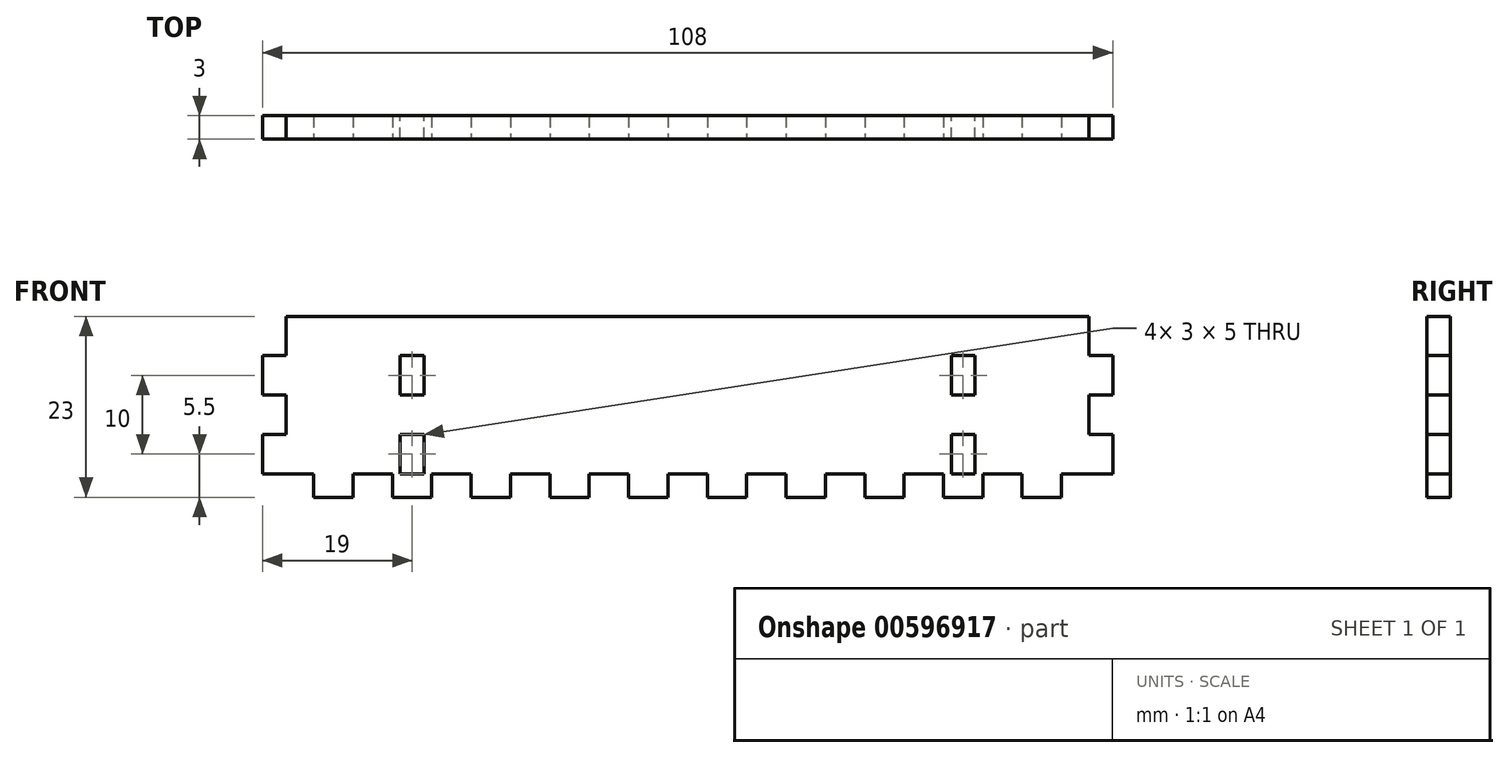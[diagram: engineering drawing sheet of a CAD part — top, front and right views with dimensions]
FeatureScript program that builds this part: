
annotation { "Feature Type Name" : "Feature", "Feature Type Description" : "" }
export const myFeature = defineFeature(function(context is Context, id is Id, definition is map)
    precondition{}
    {
        {
            var Q0;
            Q0=qCreatedBy(makeId("Front.planeOp"),FACE);
            var sketch = newSketch(context, id + "F0", { "sketchPlane" : qUnion([Q0])});
            skLineSegment(sketch, "E0.bottom", {"start": v(51, 20) * mm, "end": v(-51, 20) * mm});
            skLineSegment(sketch, "E0.top", {"start": v(51, -20) * mm, "end": v(-51, -20) * mm});
            skLineSegment(sketch, "E0.left", {"start": v(51, 20) * mm, "end": v(51, -20) * mm});
            skLineSegment(sketch, "E0.right", {"start": v(-51, 20) * mm, "end": v(-51, -20) * mm});
            skPoint(sketch, "E0.middle", {"position": v(0, 0) * mm});
            skSolve(sketch);
        }
        {
            var Q0;
            Q0=qSketchRegion(id+"F0",true);
            extrude(context, id + "F1", {"entities" : qUnion([Q0]), "depth" : 3 * mm, "offsetDistance" : 25 * mm});
        }
        {
            var Q0;
            Q0=makeQuery(id+"F1.opExtrude","CAP_FACE",FACE,{"disambiguationData":[OSD([sQuery(id+"F0.wireOp",EDGE,"E0.bottom"),sQuery(id+"F0.wireOp",EDGE,"E0.top"),sQuery(id+"F0.wireOp",EDGE,"E0.left"),sQuery(id+"F0.wireOp",EDGE,"E0.right")])],"isStart":false});
            var sketch = newSketch(context, id + "F2", { "sketchPlane" : qUnion([Q0])});
            skLineSegment(sketch, "E1.bottom", {"start": v(-51, -20) * mm, "end": v(-54, -20) * mm});
            skLineSegment(sketch, "E1.top", {"start": v(-51, -15) * mm, "end": v(-54, -15) * mm});
            skLineSegment(sketch, "E1.left", {"start": v(-51, -20) * mm, "end": v(-51, -15) * mm});
            skLineSegment(sketch, "E1.right", {"start": v(-54, -20) * mm, "end": v(-54, -15) * mm});
            skLineSegment(sketch, "E2.0.1.0", {"start": v(-51, -5) * mm, "end": v(-54, -5) * mm});
            skLineSegment(sketch, "E2.0.1.1", {"start": v(-54, -10) * mm, "end": v(-54, -5) * mm});
            skLineSegment(sketch, "E2.0.1.2", {"start": v(-51, -10) * mm, "end": v(-51, -5) * mm});
            skLineSegment(sketch, "E2.0.1.3", {"start": v(-51, -10) * mm, "end": v(-54, -10) * mm});
            skLineSegment(sketch, "E2.0.2.0", {"start": v(-51, 5) * mm, "end": v(-54, 5) * mm});
            skLineSegment(sketch, "E2.0.2.1", {"start": v(-54, 0) * mm, "end": v(-54, 5) * mm});
            skLineSegment(sketch, "E2.0.2.2", {"start": v(-51, 0) * mm, "end": v(-51, 5) * mm});
            skLineSegment(sketch, "E2.0.2.3", {"start": v(-51, 0) * mm, "end": v(-54, 0) * mm});
            skLineSegment(sketch, "E2.0.3.0", {"start": v(-51, 15) * mm, "end": v(-54, 15) * mm});
            skLineSegment(sketch, "E2.0.3.1", {"start": v(-54, 10) * mm, "end": v(-54, 15) * mm});
            skLineSegment(sketch, "E2.0.3.2", {"start": v(-51, 10) * mm, "end": v(-51, 15) * mm});
            skLineSegment(sketch, "E2.0.3.3", {"start": v(-51, 10) * mm, "end": v(-54, 10) * mm});
            skLineSegment(sketch, "E2.direction1", {"start": v(-54, -15) * mm, "end": v(-29, -15) * mm, "construction": true});
            skLineSegment(sketch, "E2.direction2", {"start": v(-54, -15) * mm, "end": v(-54, -5) * mm, "construction": true});
            skLineSegment(sketch, "E3.MirrorCS", {"start": v(54, -10) * mm, "end": v(54, -5) * mm});
            skLineSegment(sketch, "E4.MirrorCS", {"start": v(51, -5) * mm, "end": v(54, -5) * mm});
            skLineSegment(sketch, "E5.MirrorCS", {"start": v(51, -20) * mm, "end": v(51, -15) * mm});
            skLineSegment(sketch, "E6.MirrorCS", {"start": v(54, 10) * mm, "end": v(54, 15) * mm});
            skLineSegment(sketch, "E7.MirrorCS", {"start": v(51, -20) * mm, "end": v(54, -20) * mm});
            skLineSegment(sketch, "E8.MirrorCS", {"start": v(51, -15) * mm, "end": v(54, -15) * mm});
            skLineSegment(sketch, "E9.MirrorCS", {"start": v(54, -20) * mm, "end": v(54, -15) * mm});
            skLineSegment(sketch, "E10.MirrorCS", {"start": v(51, 15) * mm, "end": v(54, 15) * mm});
            skLineSegment(sketch, "E11.MirrorCS", {"start": v(51, 10) * mm, "end": v(54, 10) * mm});
            skLineSegment(sketch, "E12.MirrorCS", {"start": v(54, -15) * mm, "end": v(54, -5) * mm, "construction": true});
            skLineSegment(sketch, "E13.MirrorCS", {"start": v(51, 10) * mm, "end": v(51, 15) * mm});
            skLineSegment(sketch, "E14.MirrorCS", {"start": v(54, 0) * mm, "end": v(54, 5) * mm});
            skLineSegment(sketch, "E15.MirrorCS", {"start": v(51, 0) * mm, "end": v(51, 5) * mm});
            skLineSegment(sketch, "E16.MirrorCS", {"start": v(51, 0) * mm, "end": v(54, 0) * mm});
            skLineSegment(sketch, "E17.MirrorCS", {"start": v(51, -10) * mm, "end": v(51, -5) * mm});
            skLineSegment(sketch, "E18.MirrorCS", {"start": v(51, -10) * mm, "end": v(54, -10) * mm});
            skLineSegment(sketch, "E19.MirrorCS", {"start": v(51, 5) * mm, "end": v(54, 5) * mm});
            skSolve(sketch);
        }
        {
            var Q0;
            Q0=qSketchRegion(id+"F2",true);
            extrude(context, id + "F3", {"entities" : qUnion([Q0]), "operationType" : NewBodyOperationType.ADD, "oppositeDirection" : true, "depth" : 3 * mm, "offsetDistance" : 25 * mm});
        }
        {
            var Q0;
            Q0=makeQuery(id+"F3.boolean.opBoolean","MERGE",FACE,{"derivedFrom":[makeQuery(id+"F1.opExtrude","CAP_FACE",FACE,{"disambiguationData":[OSD([sQuery(id+"F0.wireOp",EDGE,"E0.bottom"),sQuery(id+"F0.wireOp",EDGE,"E0.top"),sQuery(id+"F0.wireOp",EDGE,"E0.left"),sQuery(id+"F0.wireOp",EDGE,"E0.right")])],"isStart":false}),makeQuery(id+"F3.opExtrude","CAP_FACE",FACE,{"disambiguationData":[OSD([sQuery(id+"F2.wireOp",EDGE,"E1.bottom"),sQuery(id+"F2.wireOp",EDGE,"E1.top"),sQuery(id+"F2.wireOp",EDGE,"E1.left"),sQuery(id+"F2.wireOp",EDGE,"E1.right")])],"isStart":true}),makeQuery(id+"F3.opExtrude","CAP_FACE",FACE,{"disambiguationData":[OSD([sQuery(id+"F2.wireOp",EDGE,"E2.0.1.0"),sQuery(id+"F2.wireOp",EDGE,"E2.0.1.1"),sQuery(id+"F2.wireOp",EDGE,"E2.0.1.2"),sQuery(id+"F2.wireOp",EDGE,"E2.0.1.3")])],"isStart":true}),makeQuery(id+"F3.opExtrude","CAP_FACE",FACE,{"disambiguationData":[OSD([sQuery(id+"F2.wireOp",EDGE,"E2.0.2.0"),sQuery(id+"F2.wireOp",EDGE,"E2.0.2.1"),sQuery(id+"F2.wireOp",EDGE,"E2.0.2.2"),sQuery(id+"F2.wireOp",EDGE,"E2.0.2.3")])],"isStart":true}),makeQuery(id+"F3.opExtrude","CAP_FACE",FACE,{"disambiguationData":[OSD([sQuery(id+"F2.wireOp",EDGE,"E2.0.3.0"),sQuery(id+"F2.wireOp",EDGE,"E2.0.3.1"),sQuery(id+"F2.wireOp",EDGE,"E2.0.3.2"),sQuery(id+"F2.wireOp",EDGE,"E2.0.3.3")])],"isStart":true}),makeQuery(id+"F3.opExtrude","CAP_FACE",FACE,{"disambiguationData":[OSD([sQuery(id+"F2.wireOp",EDGE,"E3.MirrorCS"),sQuery(id+"F2.wireOp",EDGE,"E4.MirrorCS"),sQuery(id+"F2.wireOp",EDGE,"E17.MirrorCS"),sQuery(id+"F2.wireOp",EDGE,"E18.MirrorCS")])],"isStart":true}),makeQuery(id+"F3.opExtrude","CAP_FACE",FACE,{"disambiguationData":[OSD([sQuery(id+"F2.wireOp",EDGE,"E5.MirrorCS"),sQuery(id+"F2.wireOp",EDGE,"E7.MirrorCS"),sQuery(id+"F2.wireOp",EDGE,"E8.MirrorCS"),sQuery(id+"F2.wireOp",EDGE,"E9.MirrorCS")])],"isStart":true}),makeQuery(id+"F3.opExtrude","CAP_FACE",FACE,{"disambiguationData":[OSD([sQuery(id+"F2.wireOp",EDGE,"E6.MirrorCS"),sQuery(id+"F2.wireOp",EDGE,"E10.MirrorCS"),sQuery(id+"F2.wireOp",EDGE,"E11.MirrorCS"),sQuery(id+"F2.wireOp",EDGE,"E13.MirrorCS")])],"isStart":true}),makeQuery(id+"F3.opExtrude","CAP_FACE",FACE,{"disambiguationData":[OSD([sQuery(id+"F2.wireOp",EDGE,"E14.MirrorCS"),sQuery(id+"F2.wireOp",EDGE,"E15.MirrorCS"),sQuery(id+"F2.wireOp",EDGE,"E16.MirrorCS"),sQuery(id+"F2.wireOp",EDGE,"E19.MirrorCS")])],"isStart":true})]});
            var sketch = newSketch(context, id + "F4", { "sketchPlane" : qUnion([Q0])});
            skLineSegment(sketch, "E20", {"start": v(0, -20) * mm, "end": v(0, -23) * mm, "construction": true});
            skPoint(sketch, "E20.endSnap0", {"position": v(0, -20) * mm});
            skLineSegment(sketch, "E21", {"start": v(0, -23) * mm, "end": v(2.5, -23) * mm, "construction": true});
            skLineSegment(sketch, "E22.bottom", {"start": v(2.5, -23) * mm, "end": v(7.5, -23) * mm});
            skLineSegment(sketch, "E22.top", {"start": v(2.5, -20) * mm, "end": v(7.5, -20) * mm});
            skLineSegment(sketch, "E22.left", {"start": v(2.5, -23) * mm, "end": v(2.5, -20) * mm});
            skLineSegment(sketch, "E22.right", {"start": v(7.5, -23) * mm, "end": v(7.5, -20) * mm});
            skLineSegment(sketch, "E23.1.0.0", {"start": v(12.5, -23) * mm, "end": v(17.5, -23) * mm});
            skLineSegment(sketch, "E23.1.0.1", {"start": v(12.5, -23) * mm, "end": v(12.5, -20) * mm});
            skLineSegment(sketch, "E23.1.0.2", {"start": v(17.5, -23) * mm, "end": v(17.5, -20) * mm});
            skLineSegment(sketch, "E23.1.0.3", {"start": v(12.5, -20) * mm, "end": v(17.5, -20) * mm});
            skLineSegment(sketch, "E23.2.0.0", {"start": v(22.5, -23) * mm, "end": v(27.5, -23) * mm});
            skLineSegment(sketch, "E23.2.0.1", {"start": v(22.5, -23) * mm, "end": v(22.5, -20) * mm});
            skLineSegment(sketch, "E23.2.0.2", {"start": v(27.5, -23) * mm, "end": v(27.5, -20) * mm});
            skLineSegment(sketch, "E23.2.0.3", {"start": v(22.5, -20) * mm, "end": v(27.5, -20) * mm});
            skLineSegment(sketch, "E23.3.0.0", {"start": v(32.5, -23) * mm, "end": v(37.5, -23) * mm});
            skLineSegment(sketch, "E23.3.0.1", {"start": v(32.5, -23) * mm, "end": v(32.5, -20) * mm});
            skLineSegment(sketch, "E23.3.0.2", {"start": v(37.5, -23) * mm, "end": v(37.5, -20) * mm});
            skLineSegment(sketch, "E23.3.0.3", {"start": v(32.5, -20) * mm, "end": v(37.5, -20) * mm});
            skLineSegment(sketch, "E23.4.0.0", {"start": v(42.5, -23) * mm, "end": v(47.5, -23) * mm});
            skLineSegment(sketch, "E23.4.0.1", {"start": v(42.5, -23) * mm, "end": v(42.5, -20) * mm});
            skLineSegment(sketch, "E23.4.0.2", {"start": v(47.5, -23) * mm, "end": v(47.5, -20) * mm});
            skLineSegment(sketch, "E23.4.0.3", {"start": v(42.5, -20) * mm, "end": v(47.5, -20) * mm});
            skLineSegment(sketch, "E23.direction1", {"start": v(2.5, -23) * mm, "end": v(12.5, -23) * mm, "construction": true});
            skLineSegment(sketch, "E24.MirrorCS", {"start": v(-27.5, -23) * mm, "end": v(-27.5, -20) * mm});
            skLineSegment(sketch, "E25.MirrorCS", {"start": v(-22.5, -23) * mm, "end": v(-22.5, -20) * mm});
            skLineSegment(sketch, "E26.MirrorCS", {"start": v(-17.5, -23) * mm, "end": v(-17.5, -20) * mm});
            skLineSegment(sketch, "E27.MirrorCS", {"start": v(-12.5, -23) * mm, "end": v(-12.5, -20) * mm});
            skLineSegment(sketch, "E28.MirrorCS", {"start": v(-7.5, -23) * mm, "end": v(-7.5, -20) * mm});
            skLineSegment(sketch, "E29.MirrorCS", {"start": v(-2.5, -23) * mm, "end": v(-2.5, -20) * mm});
            skLineSegment(sketch, "E30.MirrorCS", {"start": v(-32.5, -23) * mm, "end": v(-32.5, -20) * mm});
            skLineSegment(sketch, "E31.MirrorCS", {"start": v(-47.5, -23) * mm, "end": v(-47.5, -20) * mm});
            skLineSegment(sketch, "E32.MirrorCS", {"start": v(-37.5, -23) * mm, "end": v(-37.5, -20) * mm});
            skLineSegment(sketch, "E33.MirrorCS", {"start": v(-42.5, -23) * mm, "end": v(-42.5, -20) * mm});
            skLineSegment(sketch, "E34.MirrorCS", {"start": v(-2.5, -23) * mm, "end": v(-7.5, -23) * mm});
            skLineSegment(sketch, "E35.MirrorCS", {"start": v(-32.5, -20) * mm, "end": v(-37.5, -20) * mm});
            skLineSegment(sketch, "E36.MirrorCS", {"start": v(-42.5, -20) * mm, "end": v(-47.5, -20) * mm});
            skLineSegment(sketch, "E37.MirrorCS", {"start": v(-22.5, -23) * mm, "end": v(-27.5, -23) * mm});
            skLineSegment(sketch, "E38.MirrorCS", {"start": v(-12.5, -20) * mm, "end": v(-17.5, -20) * mm});
            skLineSegment(sketch, "E39.MirrorCS", {"start": v(-12.5, -23) * mm, "end": v(-17.5, -23) * mm});
            skLineSegment(sketch, "E40.MirrorCS", {"start": v(-2.5, -20) * mm, "end": v(-7.5, -20) * mm});
            skLineSegment(sketch, "E41.MirrorCS", {"start": v(-32.5, -23) * mm, "end": v(-37.5, -23) * mm});
            skLineSegment(sketch, "E42.MirrorCS", {"start": v(-22.5, -20) * mm, "end": v(-27.5, -20) * mm});
            skLineSegment(sketch, "E43.MirrorCS", {"start": v(-42.5, -23) * mm, "end": v(-47.5, -23) * mm});
            skLineSegment(sketch, "E44.MirrorCS", {"start": v(-2.5, -23) * mm, "end": v(-12.5, -23) * mm, "construction": true});
            skSolve(sketch);
        }
        {
            var Q0;
            Q0=qSketchRegion(id+"F4",true);
            extrude(context, id + "F5", {"entities" : qUnion([Q0]), "operationType" : NewBodyOperationType.ADD, "oppositeDirection" : true, "depth" : 3 * mm, "offsetDistance" : 25 * mm});
        }
        {
            var Q0;
            Q0=makeQuery(id+"F5.boolean.opBoolean","MERGE",FACE,{"derivedFrom":[makeQuery(id+"F3.boolean.opBoolean","MERGE",FACE,{"derivedFrom":[makeQuery(id+"F1.opExtrude","CAP_FACE",FACE,{"disambiguationData":[OSD([sQuery(id+"F0.wireOp",EDGE,"E0.bottom"),sQuery(id+"F0.wireOp",EDGE,"E0.top"),sQuery(id+"F0.wireOp",EDGE,"E0.left"),sQuery(id+"F0.wireOp",EDGE,"E0.right")])],"isStart":false}),makeQuery(id+"F3.opExtrude","CAP_FACE",FACE,{"disambiguationData":[OSD([sQuery(id+"F2.wireOp",EDGE,"E1.bottom"),sQuery(id+"F2.wireOp",EDGE,"E1.top"),sQuery(id+"F2.wireOp",EDGE,"E1.left"),sQuery(id+"F2.wireOp",EDGE,"E1.right")])],"isStart":true}),makeQuery(id+"F3.opExtrude","CAP_FACE",FACE,{"disambiguationData":[OSD([sQuery(id+"F2.wireOp",EDGE,"E2.0.1.0"),sQuery(id+"F2.wireOp",EDGE,"E2.0.1.1"),sQuery(id+"F2.wireOp",EDGE,"E2.0.1.2"),sQuery(id+"F2.wireOp",EDGE,"E2.0.1.3")])],"isStart":true}),makeQuery(id+"F3.opExtrude","CAP_FACE",FACE,{"disambiguationData":[OSD([sQuery(id+"F2.wireOp",EDGE,"E2.0.2.0"),sQuery(id+"F2.wireOp",EDGE,"E2.0.2.1"),sQuery(id+"F2.wireOp",EDGE,"E2.0.2.2"),sQuery(id+"F2.wireOp",EDGE,"E2.0.2.3")])],"isStart":true}),makeQuery(id+"F3.opExtrude","CAP_FACE",FACE,{"disambiguationData":[OSD([sQuery(id+"F2.wireOp",EDGE,"E2.0.3.0"),sQuery(id+"F2.wireOp",EDGE,"E2.0.3.1"),sQuery(id+"F2.wireOp",EDGE,"E2.0.3.2"),sQuery(id+"F2.wireOp",EDGE,"E2.0.3.3")])],"isStart":true}),makeQuery(id+"F3.opExtrude","CAP_FACE",FACE,{"disambiguationData":[OSD([sQuery(id+"F2.wireOp",EDGE,"E3.MirrorCS"),sQuery(id+"F2.wireOp",EDGE,"E4.MirrorCS"),sQuery(id+"F2.wireOp",EDGE,"E17.MirrorCS"),sQuery(id+"F2.wireOp",EDGE,"E18.MirrorCS")])],"isStart":true}),makeQuery(id+"F3.opExtrude","CAP_FACE",FACE,{"disambiguationData":[OSD([sQuery(id+"F2.wireOp",EDGE,"E5.MirrorCS"),sQuery(id+"F2.wireOp",EDGE,"E7.MirrorCS"),sQuery(id+"F2.wireOp",EDGE,"E8.MirrorCS"),sQuery(id+"F2.wireOp",EDGE,"E9.MirrorCS")])],"isStart":true}),makeQuery(id+"F3.opExtrude","CAP_FACE",FACE,{"disambiguationData":[OSD([sQuery(id+"F2.wireOp",EDGE,"E6.MirrorCS"),sQuery(id+"F2.wireOp",EDGE,"E10.MirrorCS"),sQuery(id+"F2.wireOp",EDGE,"E11.MirrorCS"),sQuery(id+"F2.wireOp",EDGE,"E13.MirrorCS")])],"isStart":true}),makeQuery(id+"F3.opExtrude","CAP_FACE",FACE,{"disambiguationData":[OSD([sQuery(id+"F2.wireOp",EDGE,"E14.MirrorCS"),sQuery(id+"F2.wireOp",EDGE,"E15.MirrorCS"),sQuery(id+"F2.wireOp",EDGE,"E16.MirrorCS"),sQuery(id+"F2.wireOp",EDGE,"E19.MirrorCS")])],"isStart":true})]}),makeQuery(id+"F5.opExtrude","CAP_FACE",FACE,{"disambiguationData":[OSD([sQuery(id+"F4.wireOp",EDGE,"E22.bottom"),sQuery(id+"F4.wireOp",EDGE,"E22.top"),sQuery(id+"F4.wireOp",EDGE,"E22.left"),sQuery(id+"F4.wireOp",EDGE,"E22.right")])],"isStart":true}),makeQuery(id+"F5.opExtrude","CAP_FACE",FACE,{"disambiguationData":[OSD([sQuery(id+"F4.wireOp",EDGE,"E23.1.0.0"),sQuery(id+"F4.wireOp",EDGE,"E23.1.0.1"),sQuery(id+"F4.wireOp",EDGE,"E23.1.0.2"),sQuery(id+"F4.wireOp",EDGE,"E23.1.0.3")])],"isStart":true}),makeQuery(id+"F5.opExtrude","CAP_FACE",FACE,{"disambiguationData":[OSD([sQuery(id+"F4.wireOp",EDGE,"E23.2.0.0"),sQuery(id+"F4.wireOp",EDGE,"E23.2.0.1"),sQuery(id+"F4.wireOp",EDGE,"E23.2.0.2"),sQuery(id+"F4.wireOp",EDGE,"E23.2.0.3")])],"isStart":true}),makeQuery(id+"F5.opExtrude","CAP_FACE",FACE,{"disambiguationData":[OSD([sQuery(id+"F4.wireOp",EDGE,"E23.3.0.0"),sQuery(id+"F4.wireOp",EDGE,"E23.3.0.1"),sQuery(id+"F4.wireOp",EDGE,"E23.3.0.2"),sQuery(id+"F4.wireOp",EDGE,"E23.3.0.3")])],"isStart":true}),makeQuery(id+"F5.opExtrude","CAP_FACE",FACE,{"disambiguationData":[OSD([sQuery(id+"F4.wireOp",EDGE,"E23.4.0.0"),sQuery(id+"F4.wireOp",EDGE,"E23.4.0.1"),sQuery(id+"F4.wireOp",EDGE,"E23.4.0.2"),sQuery(id+"F4.wireOp",EDGE,"E23.4.0.3")])],"isStart":true}),makeQuery(id+"F5.opExtrude","CAP_FACE",FACE,{"disambiguationData":[OSD([sQuery(id+"F4.wireOp",EDGE,"E24.MirrorCS"),sQuery(id+"F4.wireOp",EDGE,"E25.MirrorCS"),sQuery(id+"F4.wireOp",EDGE,"E37.MirrorCS"),sQuery(id+"F4.wireOp",EDGE,"E42.MirrorCS")])],"isStart":true}),makeQuery(id+"F5.opExtrude","CAP_FACE",FACE,{"disambiguationData":[OSD([sQuery(id+"F4.wireOp",EDGE,"E26.MirrorCS"),sQuery(id+"F4.wireOp",EDGE,"E27.MirrorCS"),sQuery(id+"F4.wireOp",EDGE,"E38.MirrorCS"),sQuery(id+"F4.wireOp",EDGE,"E39.MirrorCS")])],"isStart":true}),makeQuery(id+"F5.opExtrude","CAP_FACE",FACE,{"disambiguationData":[OSD([sQuery(id+"F4.wireOp",EDGE,"E28.MirrorCS"),sQuery(id+"F4.wireOp",EDGE,"E29.MirrorCS"),sQuery(id+"F4.wireOp",EDGE,"E34.MirrorCS"),sQuery(id+"F4.wireOp",EDGE,"E40.MirrorCS")])],"isStart":true}),makeQuery(id+"F5.opExtrude","CAP_FACE",FACE,{"disambiguationData":[OSD([sQuery(id+"F4.wireOp",EDGE,"E30.MirrorCS"),sQuery(id+"F4.wireOp",EDGE,"E32.MirrorCS"),sQuery(id+"F4.wireOp",EDGE,"E35.MirrorCS"),sQuery(id+"F4.wireOp",EDGE,"E41.MirrorCS")])],"isStart":true}),makeQuery(id+"F5.opExtrude","CAP_FACE",FACE,{"disambiguationData":[OSD([sQuery(id+"F4.wireOp",EDGE,"E31.MirrorCS"),sQuery(id+"F4.wireOp",EDGE,"E33.MirrorCS"),sQuery(id+"F4.wireOp",EDGE,"E36.MirrorCS"),sQuery(id+"F4.wireOp",EDGE,"E43.MirrorCS")])],"isStart":true})]});
            var sketch = newSketch(context, id + "F6", { "sketchPlane" : qUnion([Q0])});
            skLineSegment(sketch, "E45.bottom", {"start": v(-54, 0) * mm, "end": v(60.5, 0) * mm});
            skLineSegment(sketch, "E45.top", {"start": v(-54, 23.45) * mm, "end": v(60.5, 23.45) * mm});
            skLineSegment(sketch, "E45.left", {"start": v(-54, 0) * mm, "end": v(-54, 23.45) * mm});
            skLineSegment(sketch, "E45.right", {"start": v(60.5, 0) * mm, "end": v(60.5, 23.45) * mm});
            skSolve(sketch);
        }
        {
            var Q0;
            Q0 = qSketchRegion(id + "F6", true);
            extrude(context, id + "F7", {"entities" : qUnion([Q0]), "operationType" : NewBodyOperationType.REMOVE, "oppositeDirection" : true, "depth" : 25 * mm, "offsetDistance" : 25 * mm});
        }
        {
            var Q0;
            Q0=makeQuery(id+"F5.boolean.opBoolean","MERGE",FACE,{"derivedFrom":[makeQuery(id+"F3.boolean.opBoolean","MERGE",FACE,{"derivedFrom":[makeQuery(id+"F1.opExtrude","CAP_FACE",FACE,{"disambiguationData":[OSD([sQuery(id+"F0.wireOp",EDGE,"E0.bottom"),sQuery(id+"F0.wireOp",EDGE,"E0.top"),sQuery(id+"F0.wireOp",EDGE,"E0.left"),sQuery(id+"F0.wireOp",EDGE,"E0.right")])],"isStart":true}),makeQuery(id+"F3.opExtrude","CAP_FACE",FACE,{"disambiguationData":[OSD([sQuery(id+"F2.wireOp",EDGE,"E1.bottom"),sQuery(id+"F2.wireOp",EDGE,"E1.top"),sQuery(id+"F2.wireOp",EDGE,"E1.left"),sQuery(id+"F2.wireOp",EDGE,"E1.right")])],"isStart":false}),makeQuery(id+"F3.opExtrude","CAP_FACE",FACE,{"disambiguationData":[OSD([sQuery(id+"F2.wireOp",EDGE,"E2.0.1.0"),sQuery(id+"F2.wireOp",EDGE,"E2.0.1.1"),sQuery(id+"F2.wireOp",EDGE,"E2.0.1.2"),sQuery(id+"F2.wireOp",EDGE,"E2.0.1.3")])],"isStart":false}),makeQuery(id+"F3.opExtrude","CAP_FACE",FACE,{"disambiguationData":[OSD([sQuery(id+"F2.wireOp",EDGE,"E2.0.2.0"),sQuery(id+"F2.wireOp",EDGE,"E2.0.2.1"),sQuery(id+"F2.wireOp",EDGE,"E2.0.2.2"),sQuery(id+"F2.wireOp",EDGE,"E2.0.2.3")])],"isStart":false}),makeQuery(id+"F3.opExtrude","CAP_FACE",FACE,{"disambiguationData":[OSD([sQuery(id+"F2.wireOp",EDGE,"E2.0.3.0"),sQuery(id+"F2.wireOp",EDGE,"E2.0.3.1"),sQuery(id+"F2.wireOp",EDGE,"E2.0.3.2"),sQuery(id+"F2.wireOp",EDGE,"E2.0.3.3")])],"isStart":false}),makeQuery(id+"F3.opExtrude","CAP_FACE",FACE,{"disambiguationData":[OSD([sQuery(id+"F2.wireOp",EDGE,"E3.MirrorCS"),sQuery(id+"F2.wireOp",EDGE,"E4.MirrorCS"),sQuery(id+"F2.wireOp",EDGE,"E17.MirrorCS"),sQuery(id+"F2.wireOp",EDGE,"E18.MirrorCS")])],"isStart":false}),makeQuery(id+"F3.opExtrude","CAP_FACE",FACE,{"disambiguationData":[OSD([sQuery(id+"F2.wireOp",EDGE,"E5.MirrorCS"),sQuery(id+"F2.wireOp",EDGE,"E7.MirrorCS"),sQuery(id+"F2.wireOp",EDGE,"E8.MirrorCS"),sQuery(id+"F2.wireOp",EDGE,"E9.MirrorCS")])],"isStart":false}),makeQuery(id+"F3.opExtrude","CAP_FACE",FACE,{"disambiguationData":[OSD([sQuery(id+"F2.wireOp",EDGE,"E6.MirrorCS"),sQuery(id+"F2.wireOp",EDGE,"E10.MirrorCS"),sQuery(id+"F2.wireOp",EDGE,"E11.MirrorCS"),sQuery(id+"F2.wireOp",EDGE,"E13.MirrorCS")])],"isStart":false}),makeQuery(id+"F3.opExtrude","CAP_FACE",FACE,{"disambiguationData":[OSD([sQuery(id+"F2.wireOp",EDGE,"E14.MirrorCS"),sQuery(id+"F2.wireOp",EDGE,"E15.MirrorCS"),sQuery(id+"F2.wireOp",EDGE,"E16.MirrorCS"),sQuery(id+"F2.wireOp",EDGE,"E19.MirrorCS")])],"isStart":false})]}),makeQuery(id+"F5.opExtrude","CAP_FACE",FACE,{"disambiguationData":[OSD([sQuery(id+"F4.wireOp",EDGE,"E22.bottom"),sQuery(id+"F4.wireOp",EDGE,"E22.top"),sQuery(id+"F4.wireOp",EDGE,"E22.left"),sQuery(id+"F4.wireOp",EDGE,"E22.right")])],"isStart":false}),makeQuery(id+"F5.opExtrude","CAP_FACE",FACE,{"disambiguationData":[OSD([sQuery(id+"F4.wireOp",EDGE,"E23.1.0.0"),sQuery(id+"F4.wireOp",EDGE,"E23.1.0.1"),sQuery(id+"F4.wireOp",EDGE,"E23.1.0.2"),sQuery(id+"F4.wireOp",EDGE,"E23.1.0.3")])],"isStart":false}),makeQuery(id+"F5.opExtrude","CAP_FACE",FACE,{"disambiguationData":[OSD([sQuery(id+"F4.wireOp",EDGE,"E23.2.0.0"),sQuery(id+"F4.wireOp",EDGE,"E23.2.0.1"),sQuery(id+"F4.wireOp",EDGE,"E23.2.0.2"),sQuery(id+"F4.wireOp",EDGE,"E23.2.0.3")])],"isStart":false}),makeQuery(id+"F5.opExtrude","CAP_FACE",FACE,{"disambiguationData":[OSD([sQuery(id+"F4.wireOp",EDGE,"E23.3.0.0"),sQuery(id+"F4.wireOp",EDGE,"E23.3.0.1"),sQuery(id+"F4.wireOp",EDGE,"E23.3.0.2"),sQuery(id+"F4.wireOp",EDGE,"E23.3.0.3")])],"isStart":false}),makeQuery(id+"F5.opExtrude","CAP_FACE",FACE,{"disambiguationData":[OSD([sQuery(id+"F4.wireOp",EDGE,"E23.4.0.0"),sQuery(id+"F4.wireOp",EDGE,"E23.4.0.1"),sQuery(id+"F4.wireOp",EDGE,"E23.4.0.2"),sQuery(id+"F4.wireOp",EDGE,"E23.4.0.3")])],"isStart":false}),makeQuery(id+"F5.opExtrude","CAP_FACE",FACE,{"disambiguationData":[OSD([sQuery(id+"F4.wireOp",EDGE,"E24.MirrorCS"),sQuery(id+"F4.wireOp",EDGE,"E25.MirrorCS"),sQuery(id+"F4.wireOp",EDGE,"E37.MirrorCS"),sQuery(id+"F4.wireOp",EDGE,"E42.MirrorCS")])],"isStart":false}),makeQuery(id+"F5.opExtrude","CAP_FACE",FACE,{"disambiguationData":[OSD([sQuery(id+"F4.wireOp",EDGE,"E26.MirrorCS"),sQuery(id+"F4.wireOp",EDGE,"E27.MirrorCS"),sQuery(id+"F4.wireOp",EDGE,"E38.MirrorCS"),sQuery(id+"F4.wireOp",EDGE,"E39.MirrorCS")])],"isStart":false}),makeQuery(id+"F5.opExtrude","CAP_FACE",FACE,{"disambiguationData":[OSD([sQuery(id+"F4.wireOp",EDGE,"E28.MirrorCS"),sQuery(id+"F4.wireOp",EDGE,"E29.MirrorCS"),sQuery(id+"F4.wireOp",EDGE,"E34.MirrorCS"),sQuery(id+"F4.wireOp",EDGE,"E40.MirrorCS")])],"isStart":false}),makeQuery(id+"F5.opExtrude","CAP_FACE",FACE,{"disambiguationData":[OSD([sQuery(id+"F4.wireOp",EDGE,"E30.MirrorCS"),sQuery(id+"F4.wireOp",EDGE,"E32.MirrorCS"),sQuery(id+"F4.wireOp",EDGE,"E35.MirrorCS"),sQuery(id+"F4.wireOp",EDGE,"E41.MirrorCS")])],"isStart":false}),makeQuery(id+"F5.opExtrude","CAP_FACE",FACE,{"disambiguationData":[OSD([sQuery(id+"F4.wireOp",EDGE,"E31.MirrorCS"),sQuery(id+"F4.wireOp",EDGE,"E33.MirrorCS"),sQuery(id+"F4.wireOp",EDGE,"E36.MirrorCS"),sQuery(id+"F4.wireOp",EDGE,"E43.MirrorCS")])],"isStart":false})]});
            var sketch = newSketch(context, id + "F8", { "sketchPlane" : qUnion([Q0])});
            skLineSegment(sketch, "E46", {"start": v(0, 0) * mm, "end": v(-35, 0) * mm, "construction": true});
            skLineSegment(sketch, "E47", {"start": v(-35, 0) * mm, "end": v(-35, -20) * mm, "construction": true});
            skLineSegment(sketch, "E48", {"start": v(-35, -20) * mm, "end": v(-35, -17.5) * mm, "construction": true});
            skLineSegment(sketch, "E49.bottom", {"start": v(-36.5, -20) * mm, "end": v(-33.5, -20) * mm});
            skLineSegment(sketch, "E49.top", {"start": v(-36.5, -15) * mm, "end": v(-33.5, -15) * mm});
            skLineSegment(sketch, "E49.left", {"start": v(-36.5, -20) * mm, "end": v(-36.5, -15) * mm});
            skLineSegment(sketch, "E49.right", {"start": v(-33.5, -20) * mm, "end": v(-33.5, -15) * mm});
            skPoint(sketch, "E49.middle", {"position": v(-35, -17.5) * mm});
            skLineSegment(sketch, "E50", {"start": v(-35, -17.5) * mm, "end": v(-35, -7.5) * mm, "construction": true});
            skLineSegment(sketch, "E51.bottom", {"start": v(-36.5, -10) * mm, "end": v(-33.5, -10) * mm});
            skLineSegment(sketch, "E51.top", {"start": v(-36.5, -5) * mm, "end": v(-33.5, -5) * mm});
            skLineSegment(sketch, "E51.left", {"start": v(-36.5, -10) * mm, "end": v(-36.5, -5) * mm});
            skLineSegment(sketch, "E51.right", {"start": v(-33.5, -10) * mm, "end": v(-33.5, -5) * mm});
            skPoint(sketch, "E51.middle", {"position": v(-35, -7.5) * mm});
            skLineSegment(sketch, "E52.MirrorCS", {"start": v(33.5, -10) * mm, "end": v(33.5, -5) * mm});
            skPoint(sketch, "E53.MirrorP", {"position": v(35, -17.5) * mm});
            skLineSegment(sketch, "E54.MirrorCS", {"start": v(36.5, -10) * mm, "end": v(36.5, -5) * mm});
            skLineSegment(sketch, "E55.MirrorCS", {"start": v(36.5, -5) * mm, "end": v(33.5, -5) * mm});
            skLineSegment(sketch, "E56.MirrorCS", {"start": v(36.5, -10) * mm, "end": v(33.5, -10) * mm});
            skLineSegment(sketch, "E57.MirrorCS", {"start": v(35, -17.5) * mm, "end": v(35, -7.5) * mm, "construction": true});
            skPoint(sketch, "E58.MirrorP", {"position": v(35, -7.5) * mm});
            skLineSegment(sketch, "E59.MirrorCS", {"start": v(33.5, -20) * mm, "end": v(33.5, -15) * mm});
            skLineSegment(sketch, "E60.MirrorCS", {"start": v(36.5, -20) * mm, "end": v(36.5, -15) * mm});
            skLineSegment(sketch, "E61.MirrorCS", {"start": v(36.5, -15) * mm, "end": v(33.5, -15) * mm});
            skLineSegment(sketch, "E62.MirrorCS", {"start": v(36.5, -20) * mm, "end": v(33.5, -20) * mm});
            skLineSegment(sketch, "E63.MirrorCS", {"start": v(35, -20) * mm, "end": v(35, -17.5) * mm, "construction": true});
            skSolve(sketch);
        }
        {
            var Q0;
            Q0 = qSketchRegion(id + "F8", true);
            extrude(context, id + "F9", {"entities" : qUnion([Q0]), "operationType" : NewBodyOperationType.REMOVE, "oppositeDirection" : true, "depth" : 25 * mm, "offsetDistance" : 25 * mm});
        }
    });
